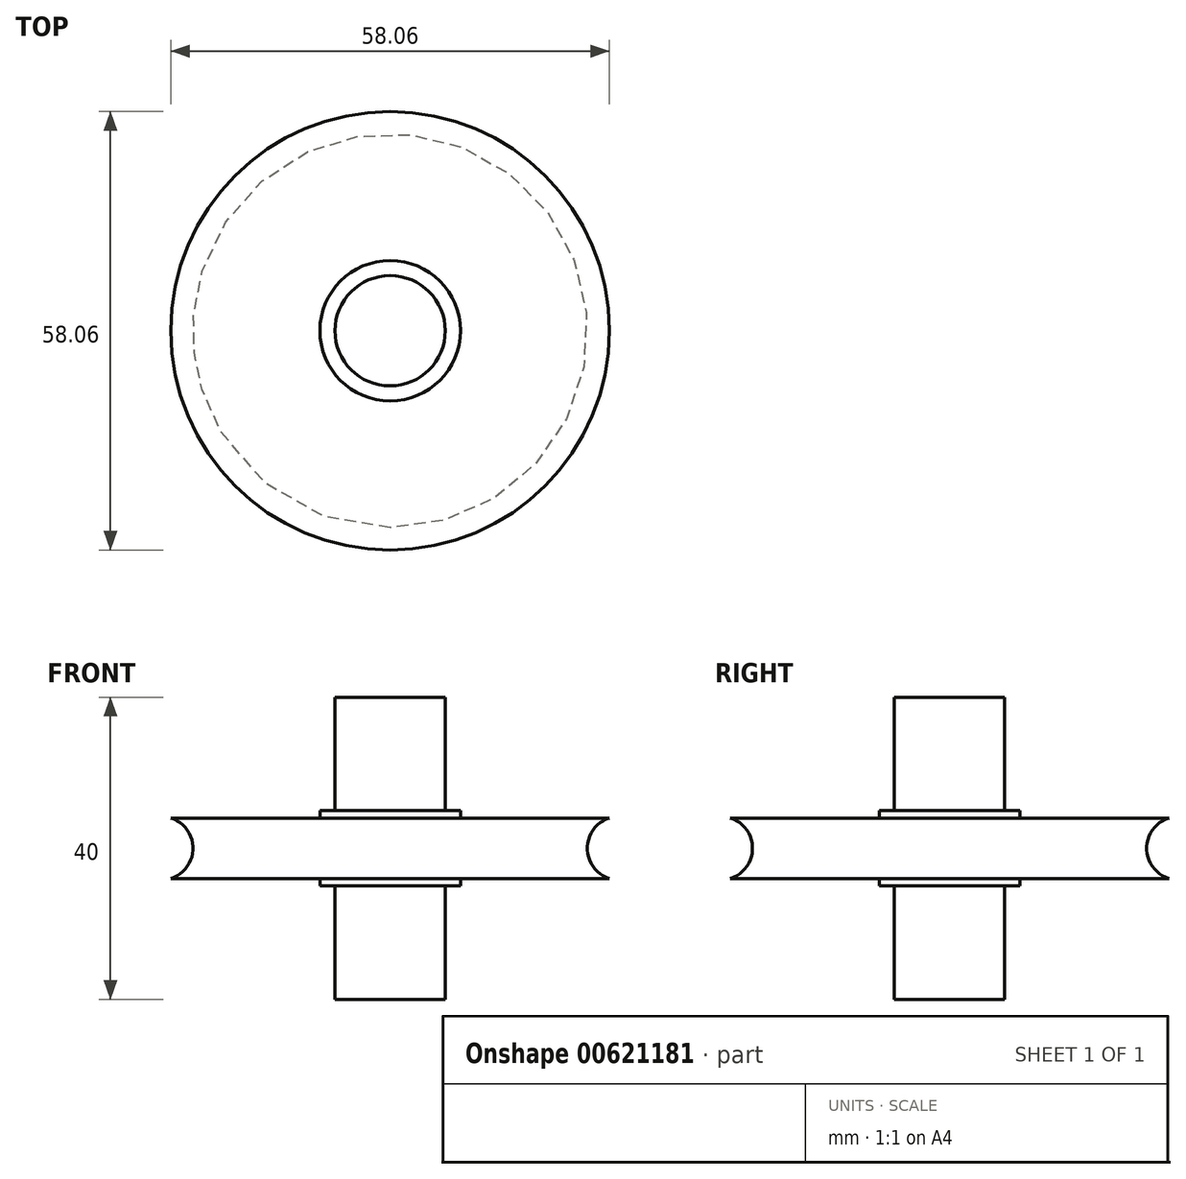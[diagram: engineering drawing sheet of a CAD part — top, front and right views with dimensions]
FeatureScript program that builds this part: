
annotation { "Feature Type Name" : "Feature", "Feature Type Description" : "" }
export const myFeature = defineFeature(function(context is Context, id is Id, definition is map)
    precondition{}
    {
        {
            var Q0;
            Q0=qCreatedBy(makeId("Top.planeOp"),FACE);
            var sketch = newSketch(context, id + "F0", { "sketchPlane" : qUnion([Q0])});
            skCircle(sketch, "E0", {"center": v(0, 0) * mm, "radius": 29.03 * mm});
            skCircle(sketch, "E1", {"center": v(0, 0) * mm, "radius": 7.3 * mm});
            skCircle(sketch, "E2.0", {"center": v(0, 0) * mm, "radius": 9.3 * mm});
            skSolve(sketch);
        }
        {
            var Q0;
            Q0=makeQuery(id+"F0.imprint","IMPRINT",FACE,{"disambiguationData":[TD([[makeQuery(id+"F0.imprint","IMPRINT",EDGE,{"derivedFrom":sQuery(id+"F0.wireOp",EDGE,"E1")}),1.0]])]});
            extrude(context, id + "F1", {"entities" : qUnion([Q0]), "endBound" : BoundingType.SYMMETRIC, "depth" : 40 * mm, "offsetDistance" : 25.4 * mm});
        }
        {
            var Q0;
            Q0=makeQuery(id+"F0.imprint","IMPRINT",FACE,{"disambiguationData":[TD([[makeQuery(id+"F0.imprint","IMPRINT",EDGE,{"derivedFrom":sQuery(id+"F0.wireOp",EDGE,"E1")}),-1.0]])]});
            extrude(context, id + "F2", {"entities" : qUnion([Q0]), "operationType" : NewBodyOperationType.ADD, "endBound" : BoundingType.SYMMETRIC, "depth" : 10 * mm, "offsetDistance" : 25 * mm});
        }
        {
            var Q0;
            Q0=makeQuery(id+"F0.imprint","IMPRINT",FACE,{"disambiguationData":[TD([[makeQuery(id+"F0.imprint","IMPRINT",EDGE,{"derivedFrom":sQuery(id+"F0.wireOp",EDGE,"E0")}),1.0]])]});
            extrude(context, id + "F3", {"entities" : qUnion([Q0]), "operationType" : NewBodyOperationType.ADD, "endBound" : BoundingType.SYMMETRIC, "depth" : 8 * mm, "offsetDistance" : 25 * mm});
        }
        {
            var Q0;
            Q0=qCreatedBy(makeId("Right.planeOp"),FACE);
            var sketch = newSketch(context, id + "F4", { "sketchPlane" : qUnion([Q0])});
            skLineSegment(sketch, "E3", {"start": v(-29.03, -4) * mm, "end": v(-29.03, 4) * mm});
            skArc(sketch, "E4", {"start": v(-29.03, -4) * mm, "mid": v(-26.1, 0) * mm, "end": v(-29.03, 4) * mm});
            skSolve(sketch);
        }
        {
            var Q0;
            Q0 = qSketchRegion(id + "F4", true);
            var Q1;
            Q1=sQuery(id+"F4.wireOp",EDGE,"E4");
            var Q2;
            Q2=makeQuery(id+"F3.opExtrude","CAP_EDGE",EDGE,{"disambiguationData":[OSD([sQuery(id+"F0.wireOp",EDGE,"E0")])],"isStart":false});
            var Q3;
            Q3=makeQuery(id+"F3.opExtrude","CAP_EDGE",EDGE,{"disambiguationData":[OSD([sQuery(id+"F0.wireOp",EDGE,"E0")])],"isStart":false});
            sweep(context, id + "F5", {"operationType" : NewBodyOperationType.REMOVE, "profiles" : qUnion([Q0]), "surfaceProfiles" : qUnion([Q1, Q2]), "path" : qUnion([Q3])});
        }
    });
